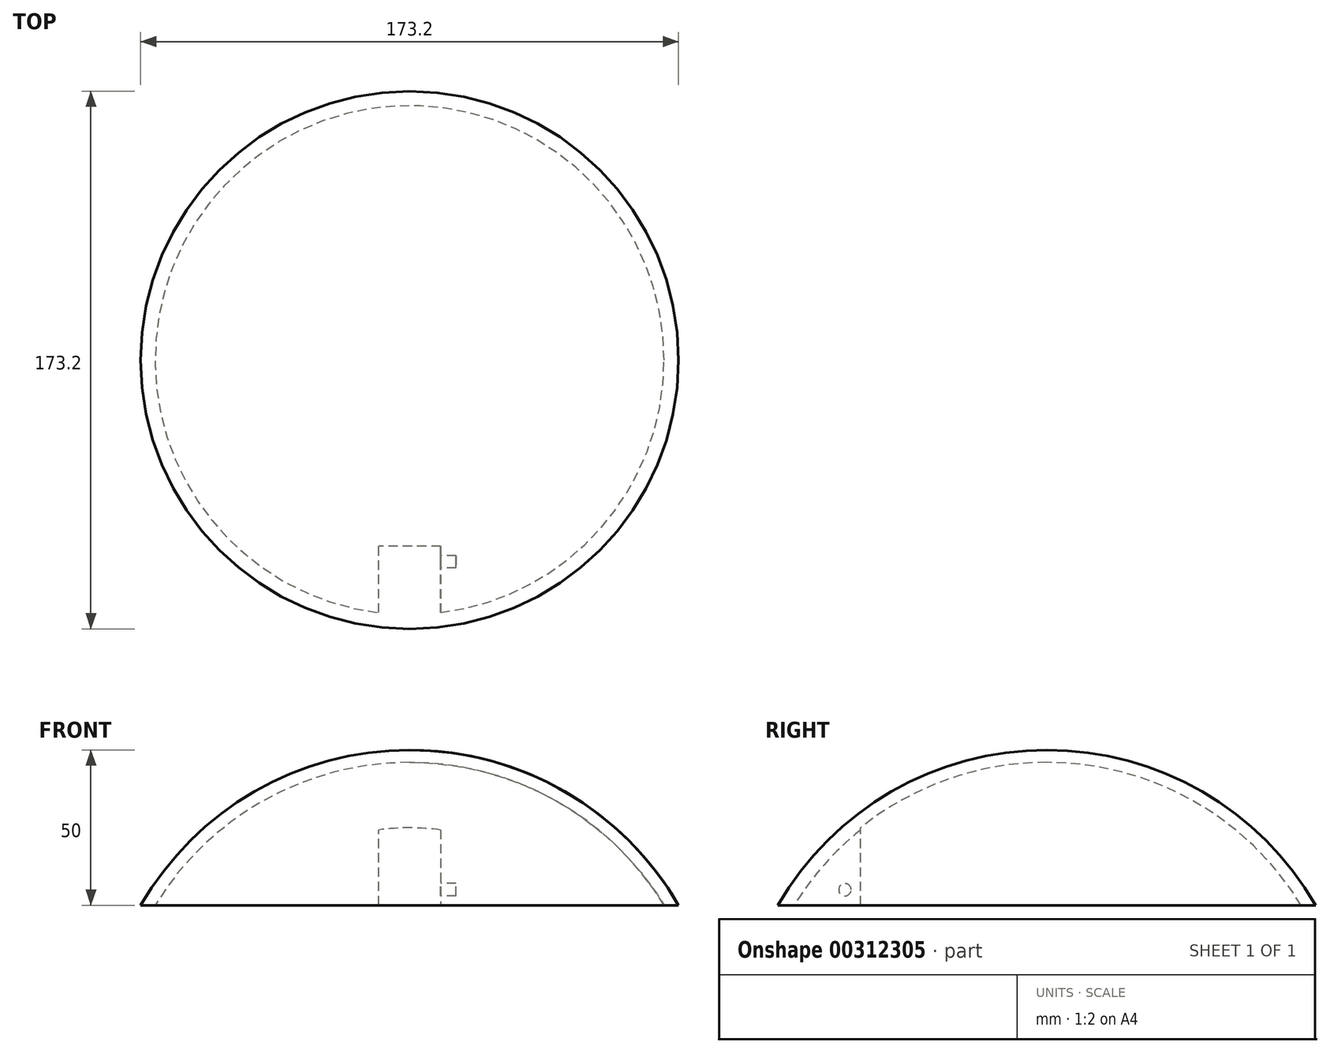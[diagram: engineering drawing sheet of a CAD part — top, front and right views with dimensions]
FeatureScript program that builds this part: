
annotation { "Feature Type Name" : "Feature", "Feature Type Description" : "" }
export const myFeature = defineFeature(function(context is Context, id is Id, definition is map)
    precondition{}
    {
        {
            var Q0;
            Q0=qCreatedBy(makeId("Front.planeOp"),FACE);
            var sketch = newSketch(context, id + "F0", { "sketchPlane" : qUnion([Q0])});
            skArc(sketch, "E0", {"start": v(-100, 0) * mm, "mid": v(0, -100) * mm, "end": v(100, 0) * mm});
            skLineSegment(sketch, "E1", {"start": v(-152.09, 0) * mm, "end": v(212.45, 0) * mm});
            skLineSegment(sketch, "E2", {"start": v(0, -135.54) * mm, "end": v(0, 121.72) * mm});
            skLineSegment(sketch, "E3", {"start": v(-115.02, 50) * mm, "end": v(140, 50) * mm});
            skArc(sketch, "E4.trimOffspring", {"start": v(86.6, 50) * mm, "mid": v(0, 100) * mm, "end": v(-86.6, 50) * mm});
            skSolve(sketch);
        }
        {
            var Q0;
            {var subQ0=sQuery(id+"F0.wireOp",EDGE,"E3");var subQ1=sQuery(id+"F0.wireOp",EDGE,"E2");var subQ2=makeQuery(id+"F0.imprint","INTERSECT",VERTEX,{"derivedFrom":[subQ1,subQ0]});Q0=makeQuery(id+"F0.imprint","IMPRINT",FACE,{"disambiguationData":[TD([[makeQuery(id+"F0.imprint","IMPRINT",EDGE,{"disambiguationData":[TD([[subQ2,-1.0]])],"derivedFrom":subQ1}),-1.0]])]});}
            var Q1;
            Q1=sQuery(id+"F0.wireOp",EDGE,"E2");
            revolve(context, id + "F1", {"entities" : qUnion([Q0]), "axis" : qUnion([Q1]), "revolveType" : RevolveType.FULL});
        }
        {
            var Q0;
            Q0=makeQuery(id+"F1.opRevolve","SWEPT_FACE",FACE,{"disambiguationData":[OSD([sQuery(id+"F0.wireOp",EDGE,"E3")])]});
            shell(context, id + "F2", {"entities" : qUnion([Q0]), "thickness" : 4 * mm});
        }
        {
            var Q0;
            Q0=qCreatedBy(makeId("Front.planeOp"),FACE);
            cPlane(context, id + "F3", {"entities" : qUnion([Q0]), "cplaneType" : CPlaneType.OFFSET, "offset" : 60 * mm, "width" : 150 * mm, "height" : 150 * mm});
        }
        {
            var Q0;
            Q0=qCreatedBy(id+"F3.planeOp",FACE);
            var sketch = newSketch(context, id + "F4", { "sketchPlane" : qUnion([Q0])});
            skLineSegment(sketch, "E5.0", {"start": v(10, 50) * mm, "end": v(-10, 50) * mm});
            skArc(sketch, "E6", {"start": v(10, 99.5) * mm, "mid": v(0, 100) * mm, "end": v(-10, 99.5) * mm});
            skLineSegment(sketch, "E7", {"start": v(-10, 50) * mm, "end": v(-10, 100) * mm});
            skLineSegment(sketch, "E8", {"start": v(-10, 100) * mm, "end": v(10, 100) * mm});
            skLineSegment(sketch, "E9", {"start": v(10, 100) * mm, "end": v(10, 50) * mm});
            skLineSegment(sketch, "E10", {"start": v(0, 50) * mm, "end": v(0, 105.48) * mm, "construction": true});
            skPoint(sketch, "E10.endSnap0", {"position": v(0, 100) * mm});
            skPoint(sketch, "E11.orphan", {"position": v(-86.6, 50) * mm});
            skPoint(sketch, "E12.orphan", {"position": v(86.6, 50) * mm});
            skSolve(sketch);
        }
        {
            var Q0;
            Q0 = qSketchRegion(id + "F4", true);
            var Q1;
            Q1=makeQuery(id+"F1.opRevolve","SWEPT_FACE",FACE,{"disambiguationData":[OSD([sQuery(id+"F0.wireOp",EDGE,"E4.trimOffspring")])]});
            extrude(context, id + "F5", {"entities" : qUnion([Q0]), "operationType" : NewBodyOperationType.ADD, "endBound" : BoundingType.UP_TO_SURFACE, "endBoundEntityFace" : qUnion([Q1]), "depth" : 25 * mm});
        }
        {
            var Q0;
            Q0=makeQuery(id+"F5.opExtrude","SWEPT_FACE",FACE,{"disambiguationData":[OSD([sQuery(id+"F4.wireOp",EDGE,"E9")])]});
            var sketch = newSketch(context, id + "F6", { "sketchPlane" : qUnion([Q0])});
            skCircle(sketch, "E13", {"center": v(-65, 55) * mm, "radius": 2 * mm});
            skSolve(sketch);
        }
        {
            var Q0;
            Q0 = qSketchRegion(id + "F6", true);
            extrude(context, id + "F7", {"entities" : qUnion([Q0]), "operationType" : NewBodyOperationType.ADD, "depth" : 5 * mm});
        }
    });
